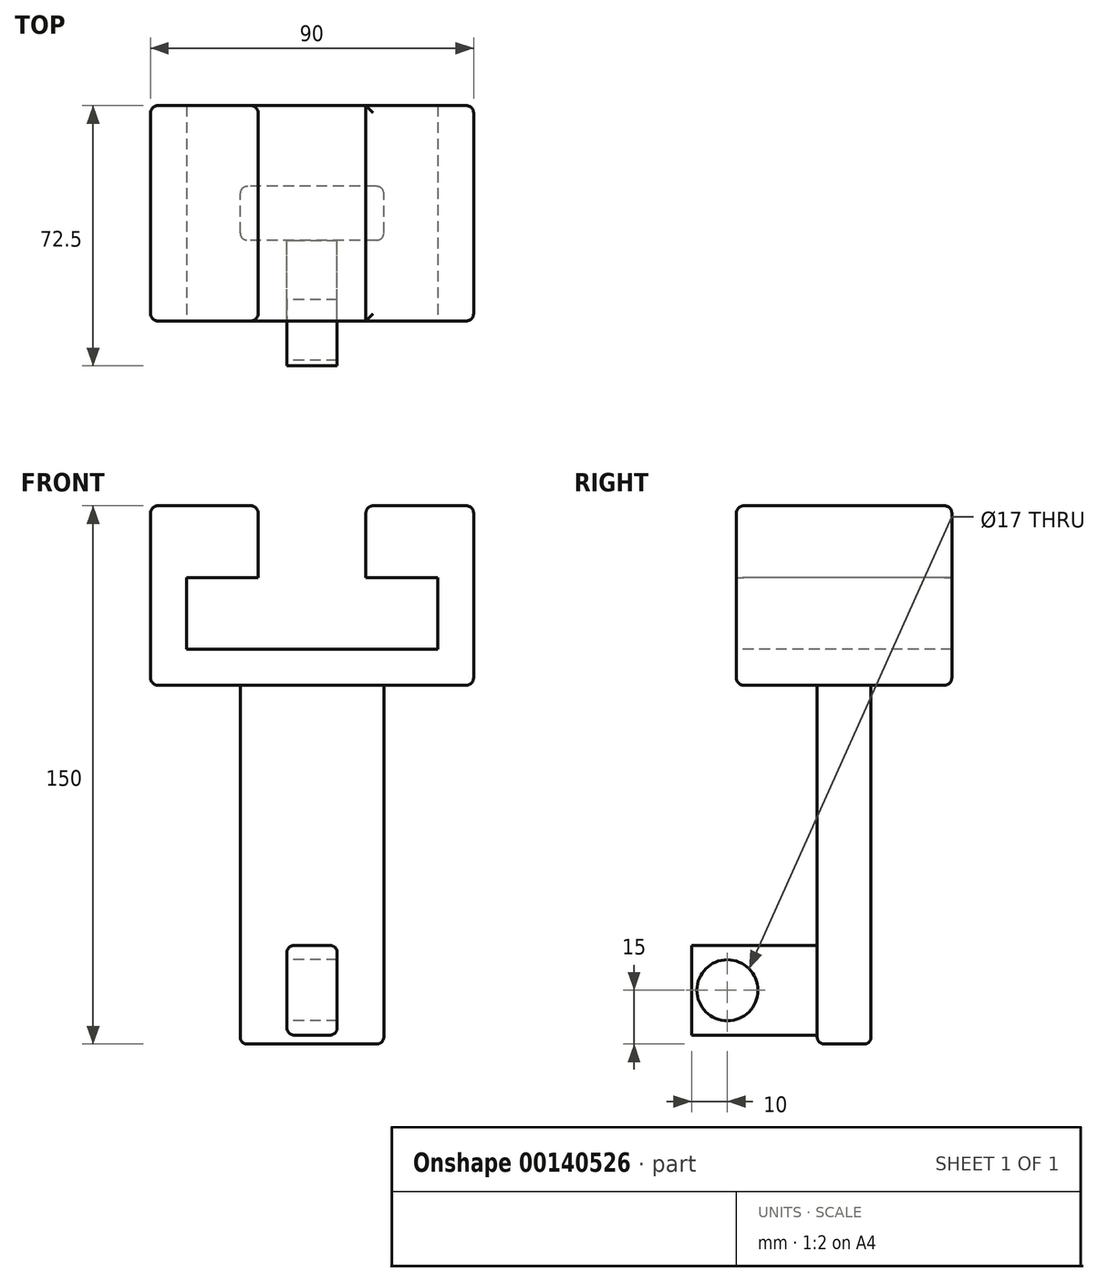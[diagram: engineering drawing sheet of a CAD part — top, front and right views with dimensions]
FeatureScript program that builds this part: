
annotation { "Feature Type Name" : "Feature", "Feature Type Description" : "" }
export const myFeature = defineFeature(function(context is Context, id is Id, definition is map)
    precondition{}
    {
        {
            var Q0;
            Q0=qCreatedBy(makeId("Top.planeOp"),FACE);
            var sketch = newSketch(context, id + "F0", { "sketchPlane" : qUnion([Q0])});
            skLineSegment(sketch, "E0.bottom", {"start": v(45, 30) * mm, "end": v(-45, 30) * mm});
            skLineSegment(sketch, "E0.top", {"start": v(45, -30) * mm, "end": v(-45, -30) * mm});
            skLineSegment(sketch, "E0.left", {"start": v(45, 30) * mm, "end": v(45, -30) * mm});
            skLineSegment(sketch, "E0.right", {"start": v(-45, 30) * mm, "end": v(-45, -30) * mm});
            skPoint(sketch, "E0.middle", {"position": v(0, 0) * mm});
            skSolve(sketch);
        }
        {
            var Q0;
            Q0 = qSketchRegion(id + "F0", true);
            extrude(context, id + "F1", {"entities" : qUnion([Q0]), "depth" : 10 * mm});
        }
        {
            var Q0;
            Q0=makeQuery(id+"F1.opExtrude","CAP_FACE",FACE,{"disambiguationData":[OSD([sQuery(id+"F0.wireOp",EDGE,"E0.bottom"),sQuery(id+"F0.wireOp",EDGE,"E0.top"),sQuery(id+"F0.wireOp",EDGE,"E0.left"),sQuery(id+"F0.wireOp",EDGE,"E0.right")])],"isStart":false});
            var sketch = newSketch(context, id + "F2", { "sketchPlane" : qUnion([Q0])});
            skLineSegment(sketch, "E1.bottom", {"start": v(-45, 30) * mm, "end": v(-35, 30) * mm});
            skLineSegment(sketch, "E1.top", {"start": v(-45, -30) * mm, "end": v(-35, -30) * mm});
            skLineSegment(sketch, "E1.left", {"start": v(-45, 30) * mm, "end": v(-45, -30) * mm});
            skLineSegment(sketch, "E1.right", {"start": v(-35, 30) * mm, "end": v(-35, -30) * mm});
            skLineSegment(sketch, "E2.bottom", {"start": v(45, 30) * mm, "end": v(35, 30) * mm});
            skLineSegment(sketch, "E2.top", {"start": v(45, -30) * mm, "end": v(35, -30) * mm});
            skLineSegment(sketch, "E2.left", {"start": v(45, 30) * mm, "end": v(45, -30) * mm});
            skLineSegment(sketch, "E2.right", {"start": v(35, 30) * mm, "end": v(35, -30) * mm});
            skSolve(sketch);
        }
        {
            var Q0;
            Q0 = qSketchRegion(id + "F2", true);
            extrude(context, id + "F3", {"entities" : qUnion([Q0]), "operationType" : NewBodyOperationType.ADD, "depth" : 20 * mm});
        }
        {
            var Q0;
            Q0=makeQuery(id+"F3.opExtrude","CAP_FACE",FACE,{"disambiguationData":[OSD([sQuery(id+"F2.wireOp",EDGE,"E1.bottom"),sQuery(id+"F2.wireOp",EDGE,"E1.top"),sQuery(id+"F2.wireOp",EDGE,"E1.left"),sQuery(id+"F2.wireOp",EDGE,"E1.right")])],"isStart":false});
            var sketch = newSketch(context, id + "F4", { "sketchPlane" : qUnion([Q0])});
            skLineSegment(sketch, "E3.bottom", {"start": v(-45, 30) * mm, "end": v(-15, 30) * mm});
            skLineSegment(sketch, "E3.top", {"start": v(-45, -30) * mm, "end": v(-15, -30) * mm});
            skLineSegment(sketch, "E3.left", {"start": v(-45, 30) * mm, "end": v(-45, -30) * mm});
            skLineSegment(sketch, "E3.right", {"start": v(-15, 30) * mm, "end": v(-15, -30) * mm});
            skSolve(sketch);
        }
        {
            var Q0;
            Q0=makeQuery(id+"F3.opExtrude","CAP_FACE",FACE,{"disambiguationData":[OSD([sQuery(id+"F2.wireOp",EDGE,"E2.bottom"),sQuery(id+"F2.wireOp",EDGE,"E2.top"),sQuery(id+"F2.wireOp",EDGE,"E2.left"),sQuery(id+"F2.wireOp",EDGE,"E2.right")])],"isStart":false});
            var sketch = newSketch(context, id + "F5", { "sketchPlane" : qUnion([Q0])});
            skLineSegment(sketch, "E4.bottom", {"start": v(45, 30) * mm, "end": v(15, 30) * mm});
            skLineSegment(sketch, "E4.top", {"start": v(45, -30) * mm, "end": v(15, -30) * mm});
            skLineSegment(sketch, "E4.left", {"start": v(45, 30) * mm, "end": v(45, -30) * mm});
            skLineSegment(sketch, "E4.right", {"start": v(15, 30) * mm, "end": v(15, -30) * mm});
            skSolve(sketch);
        }
        {
            var Q0;
            Q0 = qSketchRegion(id + "F5", true);
            extrude(context, id + "F6", {"entities" : qUnion([Q0]), "operationType" : NewBodyOperationType.ADD, "depth" : 20 * mm});
        }
        {
            var Q0;
            Q0 = qSketchRegion(id + "F4", true);
            extrude(context, id + "F7", {"entities" : qUnion([Q0]), "operationType" : NewBodyOperationType.ADD, "depth" : 20 * mm});
        }
        {
            var Q0;
            Q0=makeQuery(id+"F1.opExtrude","CAP_FACE",FACE,{"disambiguationData":[OSD([sQuery(id+"F0.wireOp",EDGE,"E0.bottom"),sQuery(id+"F0.wireOp",EDGE,"E0.top"),sQuery(id+"F0.wireOp",EDGE,"E0.left"),sQuery(id+"F0.wireOp",EDGE,"E0.right")])],"isStart":true});
            var sketch = newSketch(context, id + "F8", { "sketchPlane" : qUnion([Q0])});
            skLineSegment(sketch, "E5.bottom", {"start": v(20, 7.5) * mm, "end": v(-20, 7.5) * mm});
            skLineSegment(sketch, "E5.top", {"start": v(20, -7.5) * mm, "end": v(-20, -7.5) * mm});
            skLineSegment(sketch, "E5.left", {"start": v(20, 7.5) * mm, "end": v(20, -7.5) * mm});
            skLineSegment(sketch, "E5.right", {"start": v(-20, 7.5) * mm, "end": v(-20, -7.5) * mm});
            skPoint(sketch, "E5.middle", {"position": v(0, 0) * mm});
            skSolve(sketch);
        }
        {
            var Q0;
            Q0 = qSketchRegion(id + "F8", true);
            extrude(context, id + "F9", {"entities" : qUnion([Q0]), "operationType" : NewBodyOperationType.ADD, "depth" : 100 * mm});
        }
        {
            var Q0;
            Q0=makeQuery(id+"F9.opExtrude","SWEPT_FACE",FACE,{"disambiguationData":[OSD([sQuery(id+"F8.wireOp",EDGE,"E5.top")])]});
            var sketch = newSketch(context, id + "F10", { "sketchPlane" : qUnion([Q0])});
            skLineSegment(sketch, "E6.bottom", {"start": v(7, -72.5) * mm, "end": v(-7, -72.5) * mm});
            skLineSegment(sketch, "E6.top", {"start": v(7, -97.5) * mm, "end": v(-7, -97.5) * mm});
            skLineSegment(sketch, "E6.left", {"start": v(7, -72.5) * mm, "end": v(7, -97.5) * mm});
            skLineSegment(sketch, "E6.right", {"start": v(-7, -72.5) * mm, "end": v(-7, -97.5) * mm});
            skPoint(sketch, "E6.middle", {"position": v(0, -85) * mm});
            skSolve(sketch);
        }
        {
            var Q0;
            Q0 = qSketchRegion(id + "F10", true);
            extrude(context, id + "F11", {"entities" : qUnion([Q0]), "operationType" : NewBodyOperationType.ADD, "oppositeDirection" : true, "depth" : 50 * mm});
        }
        {
            var Q0;
            Q0=makeQuery(id+"F11.opExtrude","SWEPT_FACE",FACE,{"disambiguationData":[OSD([sQuery(id+"F10.wireOp",EDGE,"E6.left")])]});
            var sketch = newSketch(context, id + "F12", { "sketchPlane" : qUnion([Q0])});
            skCircle(sketch, "E7", {"center": v(32.5, -85) * mm, "radius": 8.5 * mm});
            skSolve(sketch);
        }
        {
            var Q0;
            Q0 = qSketchRegion(id + "F12", true);
            extrude(context, id + "F13", {"entities" : qUnion([Q0]), "operationType" : NewBodyOperationType.REMOVE, "endBound" : BoundingType.THROUGH_ALL, "oppositeDirection" : true, "depth" : 25 * mm});
        }
        {
            var Q0;
            Q0=makeQuery(id+"F9.opExtrude","SWEPT_EDGE",EDGE,{"disambiguationData":[OSD([sQuery(id+"F8.wireOp",EDGE,"E5.top"),sQuery(id+"F8.wireOp",EDGE,"E5.right")])]});
            var Q1;
            Q1=makeQuery(id+"F9.opExtrude","CAP_EDGE",EDGE,{"disambiguationData":[OSD([sQuery(id+"F8.wireOp",EDGE,"E5.top")])],"isStart":false});
            var Q2;
            Q2=makeQuery(id+"F9.opExtrude","SWEPT_EDGE",EDGE,{"disambiguationData":[OSD([sQuery(id+"F8.wireOp",EDGE,"E5.top"),sQuery(id+"F8.wireOp",EDGE,"E5.left")])]});
            var Q3;
            Q3=makeQuery(id+"F9.opExtrude","CAP_EDGE",EDGE,{"disambiguationData":[OSD([sQuery(id+"F8.wireOp",EDGE,"E5.left")])],"isStart":false});
            var Q4;
            Q4=makeQuery(id+"F9.opExtrude","CAP_EDGE",EDGE,{"disambiguationData":[OSD([sQuery(id+"F8.wireOp",EDGE,"E5.right")])],"isStart":false});
            var Q5;
            Q5=makeQuery(id+"F9.opExtrude","SWEPT_EDGE",EDGE,{"disambiguationData":[OSD([sQuery(id+"F8.wireOp",EDGE,"E5.bottom"),sQuery(id+"F8.wireOp",EDGE,"E5.right")])]});
            var Q6;
            Q6=makeQuery(id+"F9.opExtrude","SWEPT_EDGE",EDGE,{"disambiguationData":[OSD([sQuery(id+"F8.wireOp",EDGE,"E5.bottom"),sQuery(id+"F8.wireOp",EDGE,"E5.left")])]});
            var Q7;
            Q7=makeQuery(id+"F9.opExtrude","CAP_EDGE",EDGE,{"disambiguationData":[OSD([sQuery(id+"F8.wireOp",EDGE,"E5.left")])],"isStart":true});
            var Q8;
            Q8=makeQuery(id+"F9.opExtrude","CAP_EDGE",EDGE,{"disambiguationData":[OSD([sQuery(id+"F8.wireOp",EDGE,"E5.bottom")])],"isStart":false});
            var Q9;
            Q9=makeQuery(id+"F1.opExtrude","CAP_EDGE",EDGE,{"disambiguationData":[OSD([sQuery(id+"F0.wireOp",EDGE,"E0.bottom")])],"isStart":true});
            var Q10;
            Q10=makeQuery(id+"F6.boolean.opBoolean","MERGE",EDGE,{"derivedFrom":[makeQuery(id+"F3.boolean.opBoolean","MERGE",EDGE,{"derivedFrom":[makeQuery(id+"F1.opExtrude","SWEPT_EDGE",EDGE,{"disambiguationData":[OSD([sQuery(id+"F0.wireOp",EDGE,"E0.bottom"),sQuery(id+"F0.wireOp",EDGE,"E0.left")])]}),makeQuery(id+"F3.opExtrude","SWEPT_EDGE",EDGE,{"disambiguationData":[OSD([sQuery(id+"F2.wireOp",EDGE,"E2.bottom"),sQuery(id+"F2.wireOp",EDGE,"E2.left")])]})]}),makeQuery(id+"F6.opExtrude","SWEPT_EDGE",EDGE,{"disambiguationData":[OSD([sQuery(id+"F5.wireOp",EDGE,"E4.bottom"),sQuery(id+"F5.wireOp",EDGE,"E4.left")])]})]});
            var Q11;
            Q11=makeQuery(id+"F6.opExtrude","CAP_EDGE",EDGE,{"disambiguationData":[OSD([sQuery(id+"F5.wireOp",EDGE,"E4.bottom")])],"isStart":false});
            var Q12;
            Q12=makeQuery(id+"F7.opExtrude","SWEPT_EDGE",EDGE,{"disambiguationData":[OSD([sQuery(id+"F4.wireOp",EDGE,"E3.bottom"),sQuery(id+"F4.wireOp",EDGE,"E3.right")])]});
            var Q13;
            Q13=makeQuery(id+"F7.opExtrude","CAP_EDGE",EDGE,{"disambiguationData":[OSD([sQuery(id+"F4.wireOp",EDGE,"E3.bottom")])],"isStart":false});
            var Q14;
            Q14=makeQuery(id+"F7.boolean.opBoolean","MERGE",EDGE,{"derivedFrom":[makeQuery(id+"F3.boolean.opBoolean","MERGE",EDGE,{"derivedFrom":[makeQuery(id+"F1.opExtrude","SWEPT_EDGE",EDGE,{"disambiguationData":[OSD([sQuery(id+"F0.wireOp",EDGE,"E0.bottom"),sQuery(id+"F0.wireOp",EDGE,"E0.right")])]}),makeQuery(id+"F3.opExtrude","SWEPT_EDGE",EDGE,{"disambiguationData":[OSD([sQuery(id+"F2.wireOp",EDGE,"E1.bottom"),sQuery(id+"F2.wireOp",EDGE,"E1.left")])]})]}),makeQuery(id+"F7.opExtrude","SWEPT_EDGE",EDGE,{"disambiguationData":[OSD([sQuery(id+"F4.wireOp",EDGE,"E3.bottom"),sQuery(id+"F4.wireOp",EDGE,"E3.left")])]})]});
            var Q15;
            Q15=makeQuery(id+"F1.opExtrude","CAP_EDGE",EDGE,{"disambiguationData":[OSD([sQuery(id+"F0.wireOp",EDGE,"E0.right")])],"isStart":true});
            var Q16;
            Q16=makeQuery(id+"F7.opExtrude","CAP_EDGE",EDGE,{"disambiguationData":[OSD([sQuery(id+"F4.wireOp",EDGE,"E3.left")])],"isStart":false});
            var Q17;
            Q17=makeQuery(id+"F7.boolean.opBoolean","MERGE",EDGE,{"derivedFrom":[makeQuery(id+"F3.boolean.opBoolean","MERGE",EDGE,{"derivedFrom":[makeQuery(id+"F1.opExtrude","SWEPT_EDGE",EDGE,{"disambiguationData":[OSD([sQuery(id+"F0.wireOp",EDGE,"E0.top"),sQuery(id+"F0.wireOp",EDGE,"E0.right")])]}),makeQuery(id+"F3.opExtrude","SWEPT_EDGE",EDGE,{"disambiguationData":[OSD([sQuery(id+"F2.wireOp",EDGE,"E1.top"),sQuery(id+"F2.wireOp",EDGE,"E1.left")])]})]}),makeQuery(id+"F7.opExtrude","SWEPT_EDGE",EDGE,{"disambiguationData":[OSD([sQuery(id+"F4.wireOp",EDGE,"E3.top"),sQuery(id+"F4.wireOp",EDGE,"E3.left")])]})]});
            var Q18;
            Q18=makeQuery(id+"F1.opExtrude","CAP_EDGE",EDGE,{"disambiguationData":[OSD([sQuery(id+"F0.wireOp",EDGE,"E0.top")])],"isStart":true});
            var Q19;
            Q19=makeQuery(id+"F1.opExtrude","CAP_EDGE",EDGE,{"disambiguationData":[OSD([sQuery(id+"F0.wireOp",EDGE,"E0.left")])],"isStart":true});
            var Q20;
            Q20=makeQuery(id+"F6.boolean.opBoolean","MERGE",EDGE,{"derivedFrom":[makeQuery(id+"F3.boolean.opBoolean","MERGE",EDGE,{"derivedFrom":[makeQuery(id+"F1.opExtrude","SWEPT_EDGE",EDGE,{"disambiguationData":[OSD([sQuery(id+"F0.wireOp",EDGE,"E0.top"),sQuery(id+"F0.wireOp",EDGE,"E0.left")])]}),makeQuery(id+"F3.opExtrude","SWEPT_EDGE",EDGE,{"disambiguationData":[OSD([sQuery(id+"F2.wireOp",EDGE,"E2.top"),sQuery(id+"F2.wireOp",EDGE,"E2.left")])]})]}),makeQuery(id+"F6.opExtrude","SWEPT_EDGE",EDGE,{"disambiguationData":[OSD([sQuery(id+"F5.wireOp",EDGE,"E4.top"),sQuery(id+"F5.wireOp",EDGE,"E4.left")])]})]});
            var Q21;
            Q21=makeQuery(id+"F6.opExtrude","CAP_EDGE",EDGE,{"disambiguationData":[OSD([sQuery(id+"F5.wireOp",EDGE,"E4.left")])],"isStart":false});
            var Q22;
            Q22=makeQuery(id+"F6.opExtrude","CAP_EDGE",EDGE,{"disambiguationData":[OSD([sQuery(id+"F5.wireOp",EDGE,"E4.top")])],"isStart":false});
            var Q23;
            Q23=makeQuery(id+"F7.opExtrude","SWEPT_EDGE",EDGE,{"disambiguationData":[OSD([sQuery(id+"F4.wireOp",EDGE,"E3.top"),sQuery(id+"F4.wireOp",EDGE,"E3.right")])]});
            var Q24;
            Q24=makeQuery(id+"F7.opExtrude","CAP_EDGE",EDGE,{"disambiguationData":[OSD([sQuery(id+"F4.wireOp",EDGE,"E3.top")])],"isStart":false});
            var Q25;
            Q25=makeQuery(id+"F7.opExtrude","CAP_EDGE",EDGE,{"disambiguationData":[OSD([sQuery(id+"F4.wireOp",EDGE,"E3.right")])],"isStart":false});
            var Q26;
            Q26=makeQuery(id+"F6.opExtrude","CAP_EDGE",EDGE,{"disambiguationData":[OSD([sQuery(id+"F5.wireOp",EDGE,"E4.right")])],"isStart":false});
            var Q27;
            Q27=makeQuery(id+"F11.opExtrude","SWEPT_EDGE",EDGE,{"disambiguationData":[OSD([sQuery(id+"F10.wireOp",EDGE,"E6.top"),sQuery(id+"F10.wireOp",EDGE,"E6.left")])]});
            var Q28;
            Q28=makeQuery(id+"F11.opExtrude","SWEPT_EDGE",EDGE,{"disambiguationData":[OSD([sQuery(id+"F10.wireOp",EDGE,"E6.bottom"),sQuery(id+"F10.wireOp",EDGE,"E6.left")])]});
            var Q29;
            Q29=makeQuery(id+"F11.opExtrude","SWEPT_EDGE",EDGE,{"disambiguationData":[OSD([sQuery(id+"F10.wireOp",EDGE,"E6.top"),sQuery(id+"F10.wireOp",EDGE,"E6.right")])]});
            var Q30;
            Q30=makeQuery(id+"F11.opExtrude","SWEPT_EDGE",EDGE,{"disambiguationData":[OSD([sQuery(id+"F10.wireOp",EDGE,"E6.bottom"),sQuery(id+"F10.wireOp",EDGE,"E6.right")])]});
            fillet(context, id + "F14", {"entities" : qUnion([Q0, Q1, Q2, Q3, Q4, Q5, Q6, Q7, Q8, Q9, Q10, Q11, Q12, Q13, Q14, Q15, Q16, Q17, Q18, Q19, Q20, Q21, Q22, Q23, Q24, Q25, Q26, Q27, Q28, Q29, Q30]), "radius" : 2 * mm, "tangentPropagation" : true, "allowEdgeOverflow" : false});
        }
    });
